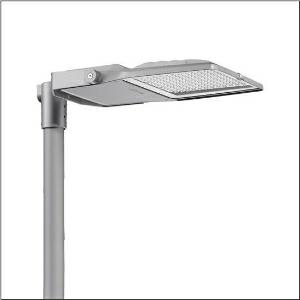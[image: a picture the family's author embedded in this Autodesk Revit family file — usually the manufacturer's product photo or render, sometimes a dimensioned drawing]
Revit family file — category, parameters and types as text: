
# Revit family: floodlight_fl_21_midi___pl43_5xa7785f2a3a_ea2c
name_source: partatom
category: Lighting Fixtures
units: mm (PartAtom-declared; Revit-internal decimal feet)

## family parameters
Cut with Voids When Loaded = No
Host = Face
Light Source = No
Part Type = Normal
Room Calculation Point = No
Round Connector Dimension = Use Diameter
Shared = No

## types (1)
- --- (1 x LED, 36680 lm, 271.6 W, 3000K)
    Apparent Load = 272 VA
    CIE Flux Codes = 27 78 99 100 100
    Color Rendering = 70
    Color Temperature = 3000K
    Default Elevation = 1800 mm
    Description = Floodlight FL 21 midi, floodlight, primary light control with lens, of PMMA, primary optical cover: protective disc, of toughened safety glass, transparent, light distribution: PL43, light emission: direct distribution, installation type: surface-mounted, LED, High Power LED, rated luminous flux: 36.680lm, luminous efficacy: 135lm/W, light colour: 730, colour temperature: 3000K, control gear: Smart Interface (Zhaga), control: flexible luminous flux parameterisation, time-dependent luminous flux control, constant luminous flux control, overheat protection, pre-setting: logarithmic dimming characteristic, with terminal, 6-pole, mains connection: 220..240V, AC, 50/60Hz, start of lifetime: 272W, end of service life: 287W, reduction: 123W, luminaire housing, of diecast aluminium, powder-coated, Siteco® metallic grey (DB 702S), corrosivity category C5 mid according to DIN EN ISO 12944, suitable for swimming pools, chlorine-resistant, sealing non-destructively replaceable, please order mast flange separately, mast bracket, of steel, galvanised, powder-coated, Siteco® metallic grey (DB 702S), Smart Interface above, protection rating (complete): IP66, insulation class (complete): insulation class II (safety insulation), certification: CE, ENEC, VDE, protection symbol: D, impact resistance: IK08, permissible operating ambient temperature: -40..+40°C, permissible operating ambient temperature for outdoor applications: -40..+50°C, standard: DIN EN 12944, LABS conformity tested according to VDMA 24364:2018-05, packaging unit: 1 piece

Light Distribution: PL43
    Height = 76 mm
    Lamp = 1 x LED
    Lamp Light Flux = 36680 lm
    Lamp Power = 271.6 W
    Lamp count = 1
    Length = 657 mm
    Luminous efficacy = 135 lm/W
    Manufacturer = Siteco
    ModVariant = No
    Model = 5XA7785F2A3A
    Number of Poles = 1
    OnlyDefault = Yes
    Power Factor = 1
    Product Name = Floodlight FL 21 midi | PL43
    Product group = floodlight | pylon annexe
    ProductGroupID = 6200
    Protection Class = Protection class II
    Protection Degree = IP 66
    RLX_Detail_Level = 1
    RLX_Emergency_Light_Flux = 0 lm
    RLX_Emergency_Type = 0
    RLX_Emergency_Type_DB = No
    RlxData = <blob elided: 153645 chars, md5=309a59f9>
    Socket = socket
    Standby Power = 0 W
    System Light Flux = 36680 lm
    System Power = 272 W
    Type Comments = factory setting: luminous flux: 100 % | dim-lin: 254 | 620 mA
    Type Image = l_1007123.jpg
    URL = http://relux.com
    VarID = @adj_177174
    Voltage = 0 V
    Weight = 0.00 kg
    Width = 442 mm

## geometry (parser evidence)
native form markers: Blend x4, Sweep x13
no freeform markers — native parametric forms only
